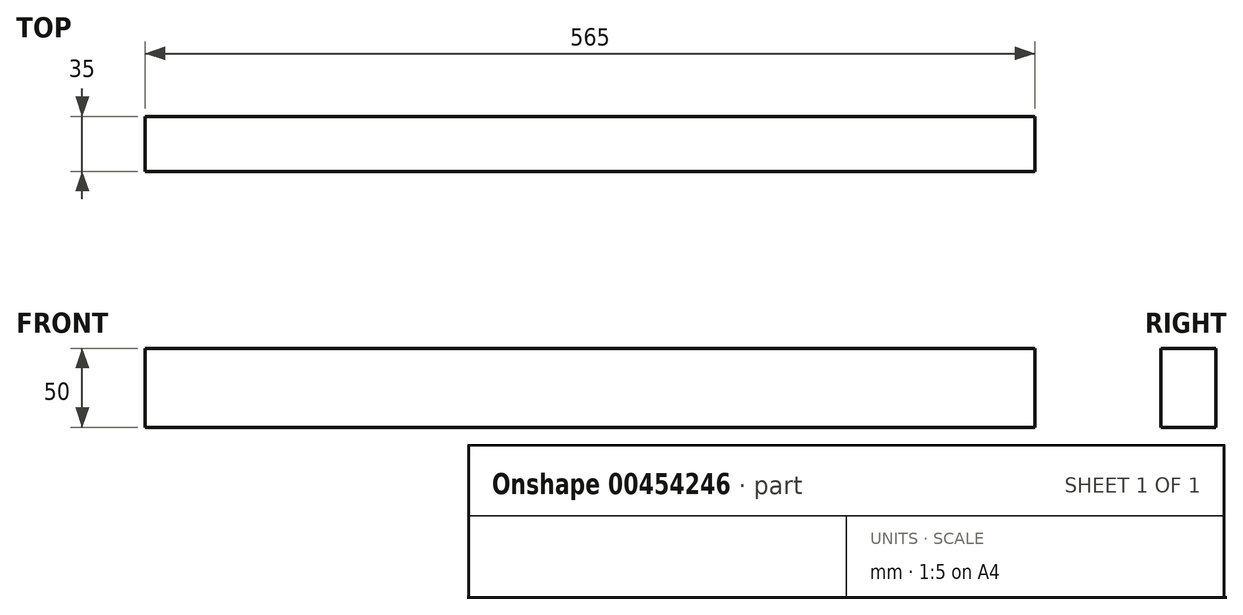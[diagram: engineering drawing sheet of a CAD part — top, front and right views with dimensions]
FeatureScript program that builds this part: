
annotation { "Feature Type Name" : "Feature", "Feature Type Description" : "" }
export const myFeature = defineFeature(function(context is Context, id is Id, definition is map)
    precondition{}
    {
        {
            var Q0;
            Q0=qCreatedBy(makeId("Front.planeOp"),FACE);
            var sketch = newSketch(context, id + "F0", { "sketchPlane" : qUnion([Q0])});
            skLineSegment(sketch, "E0.bottom", {"start": v(-282.5, 25) * mm, "end": v(282.5, 25) * mm});
            skLineSegment(sketch, "E0.top", {"start": v(-282.5, -25) * mm, "end": v(282.5, -25) * mm});
            skLineSegment(sketch, "E0.left", {"start": v(-282.5, 25) * mm, "end": v(-282.5, -25) * mm});
            skLineSegment(sketch, "E0.right", {"start": v(282.5, 25) * mm, "end": v(282.5, -25) * mm});
            skPoint(sketch, "E0.middle", {"position": v(0, 0) * mm});
            skSolve(sketch);
        }
        {
            var Q0;
            Q0=makeQuery(id+"F0.imprint","IMPRINT",FACE,{"disambiguationData":[TD([[makeQuery(id+"F0.imprint","IMPRINT",EDGE,{"derivedFrom":sQuery(id+"F0.wireOp",EDGE,"E0.bottom")}),-1.0]])]});
            extrude(context, id + "F1", {"entities" : qUnion([Q0]), "depth" : 35 * mm});
        }
    });
